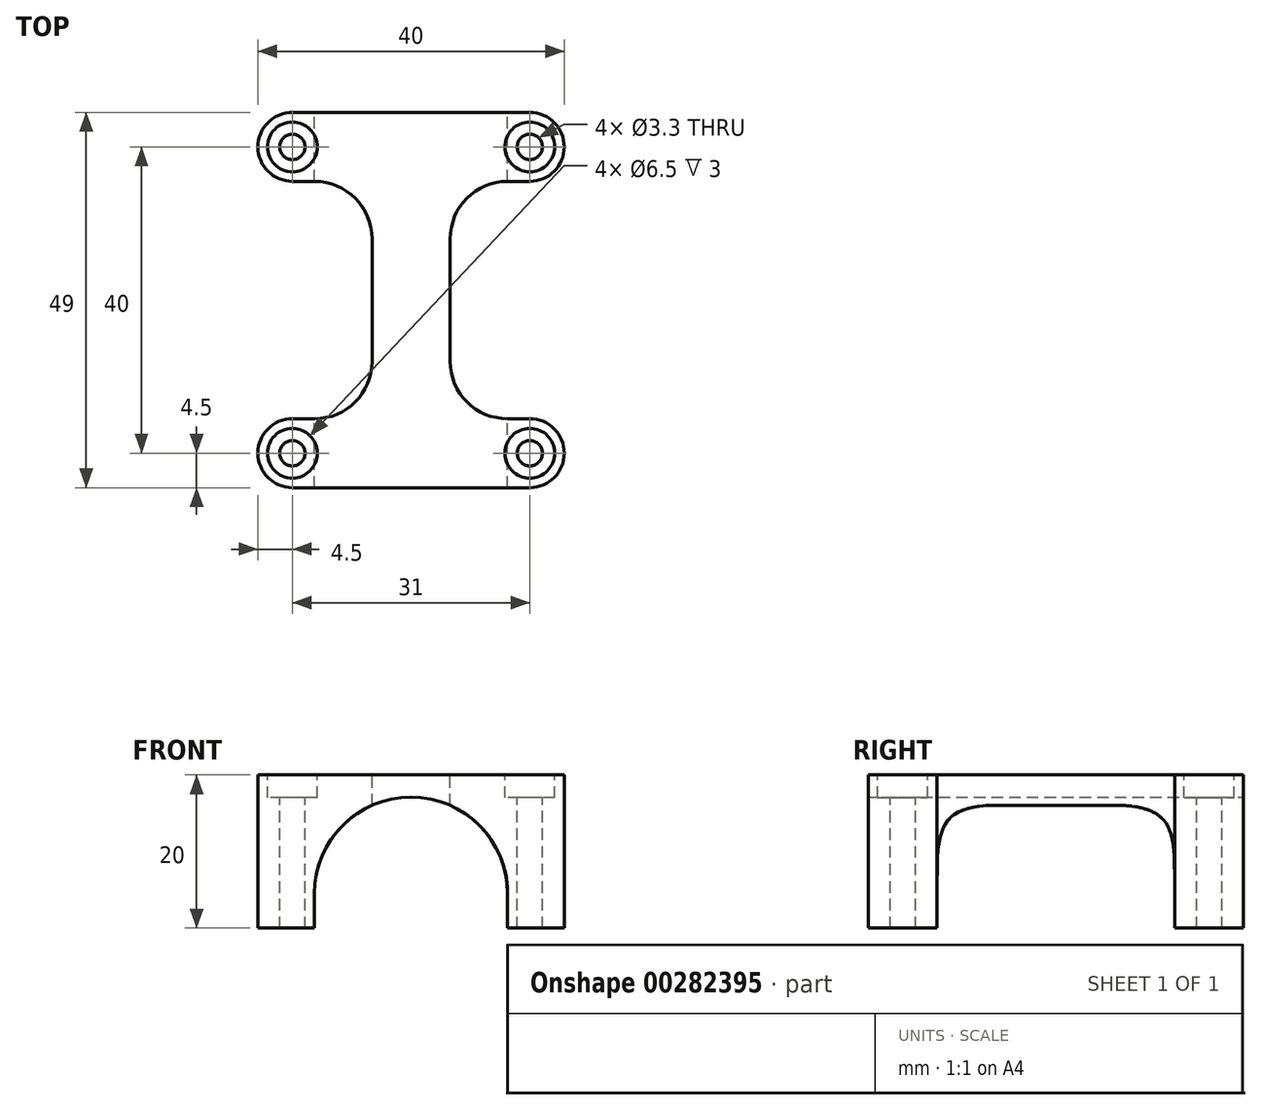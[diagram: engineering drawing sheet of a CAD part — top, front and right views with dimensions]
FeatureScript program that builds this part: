
annotation { "Feature Type Name" : "Feature", "Feature Type Description" : "" }
export const myFeature = defineFeature(function(context is Context, id is Id, definition is map)
    precondition{}
    {
        {
            var Q0;
            Q0=qCreatedBy(makeId("Front.planeOp"),FACE);
            var sketch = newSketch(context, id + "F0", { "sketchPlane" : qUnion([Q0])});
            skLineSegment(sketch, "E0.bottom", {"start": v(0, 0) * mm, "end": v(7.4, 0) * mm});
            skLineSegment(sketch, "E0.top", {"start": v(0, 20) * mm, "end": v(40, 20) * mm});
            skLineSegment(sketch, "E0.left", {"start": v(0, 0) * mm, "end": v(0, 20) * mm});
            skLineSegment(sketch, "E0.right", {"start": v(40, 0) * mm, "end": v(40, 20) * mm});
            skLineSegment(sketch, "E1", {"start": v(20, 20) * mm, "end": v(20, 4.5) * mm, "construction": true});
            skPoint(sketch, "E1.endSnap0", {"position": v(20, 0) * mm});
            skArc(sketch, "E2", {"start": v(32.6, 4.5) * mm, "mid": v(20, 17.1) * mm, "end": v(7.4, 4.5) * mm});
            skLineSegment(sketch, "E3.trimOffspring", {"start": v(32.6, 0) * mm, "end": v(40, 0) * mm});
            skLineSegment(sketch, "E4", {"start": v(7.4, 4.5) * mm, "end": v(7.4, 0) * mm});
            skLineSegment(sketch, "E5", {"start": v(32.6, 4.5) * mm, "end": v(32.6, 0) * mm});
            skSolve(sketch);
        }
        {
            var Q0;
            Q0=qSketchRegion(id+"F0",true);
            extrude(context, id + "F1", {"entities" : qUnion([Q0]), "depth" : 49 * mm});
        }
        {
            var Q0;
            Q0=makeQuery(id+"F1.opExtrude","SWEPT_FACE",FACE,{"disambiguationData":[OSD([sQuery(id+"F0.wireOp",EDGE,"E0.top")])]});
            var sketch = newSketch(context, id + "F2", { "sketchPlane" : qUnion([Q0])});
            skLineSegment(sketch, "E6", {"start": v(0, -24.5) * mm, "end": v(40, -24.5) * mm, "construction": true});
            skLineSegment(sketch, "E7", {"start": v(4.5, 0) * mm, "end": v(4.5, -49) * mm, "construction": true});
            skLineSegment(sketch, "E8", {"start": v(35.5, 0) * mm, "end": v(35.5, -49) * mm, "construction": true});
            skPoint(sketch, "E9", {"position": v(4.5, -4.5) * mm});
            skPoint(sketch, "E10", {"position": v(35.5, -4.5) * mm});
            skPoint(sketch, "E11", {"position": v(35.5, -44.5) * mm});
            skPoint(sketch, "E12", {"position": v(4.5, -44.5) * mm});
            skSolve(sketch);
        }
        {
            var Q0;
            Q0=sQuery(id+"F2.wireOp",VERTEX,"E9");
            var Q1;
            Q1=sQuery(id+"F2.wireOp",VERTEX,"E12");
            var Q2;
            Q2=sQuery(id+"F2.wireOp",VERTEX,"E11");
            var Q3;
            Q3=sQuery(id+"F2.wireOp",VERTEX,"E10");
            var Q4;
            Q4=makeQuery(id+"F1.opExtrude","SWEPT_BODY",BODY,{"disambiguationData":[OSD([sQuery(id+"F0.wireOp",EDGE,"E0.bottom"),sQuery(id+"F0.wireOp",EDGE,"E0.top"),sQuery(id+"F0.wireOp",EDGE,"E0.left"),sQuery(id+"F0.wireOp",EDGE,"E0.right"),sQuery(id+"F0.wireOp",EDGE,"E2"),sQuery(id+"F0.wireOp",EDGE,"E3.trimOffspring")])]});
            hole(context, id + "F3", {"style" : HoleStyle.C_BORE, "endStyle" : HoleEndStyle.BLIND, "standardTappedOrClearance" : lookupTablePath({ "standard" : "ISO", "fit" : "Normal", "size" : "M3", "type" : "Clearance" }), "standardBlindInLast" : lookupTablePath({ "fit" : "Standard", "standard" : "ISO", "size" : "M3", "type" : "Clearance" }), "holeDiameter" : 3.3 * mm, "cBoreDiameter" : 6.5 * mm, "cBoreDepth" : 3 * mm, "holeDepth" : 30 * mm, "tappedDepth" : 3 * mm, "tapClearance" : 3, "startFromSketch" : true, "locations" : qUnion([Q0, Q1, Q2, Q3]), "scope" : qUnion([Q4])});
        }
        {
            var Q0;
            Q0=makeQuery(id+"F1.opExtrude","SWEPT_FACE",FACE,{"disambiguationData":[OSD([sQuery(id+"F0.wireOp",EDGE,"E0.top")])]});
            var sketch = newSketch(context, id + "F4", { "sketchPlane" : qUnion([Q0])});
            skArc(sketch, "E13", {"start": v(14.9, -16.5) * mm, "mid": v(12.7, -11.2) * mm, "end": v(7.4, -9) * mm});
            skArc(sketch, "E14", {"start": v(7.4, -40) * mm, "mid": v(12.7, -37.8) * mm, "end": v(14.9, -32.5) * mm});
            skLineSegment(sketch, "E15", {"start": v(20, 0) * mm, "end": v(20, -49) * mm, "construction": true});
            skLineSegment(sketch, "E16", {"start": v(-0.1, -9) * mm, "end": v(-0.1, -40) * mm});
            skLineSegment(sketch, "E17", {"start": v(14.9, -16.5) * mm, "end": v(14.9, -32.5) * mm});
            skLineSegment(sketch, "E18", {"start": v(7.4, -16.5) * mm, "end": v(7.4, -32.5) * mm, "construction": true});
            skLineSegment(sketch, "E19", {"start": v(7.4, -9) * mm, "end": v(-0.1, -9) * mm});
            skLineSegment(sketch, "E20", {"start": v(7.4, -40) * mm, "end": v(-0.1, -40) * mm});
            skPoint(sketch, "E21.orphan", {"position": v(-0.1, -16.5) * mm});
            skPoint(sketch, "E22.orphan", {"position": v(-0.1, -32.5) * mm});
            skArc(sketch, "E23.MirrorCS", {"start": v(25.1, -16.5) * mm, "mid": v(27.3, -11.2) * mm, "end": v(32.6, -9) * mm});
            skLineSegment(sketch, "E24.MirrorCS", {"start": v(25.1, -16.5) * mm, "end": v(25.1, -32.5) * mm});
            skArc(sketch, "E25.MirrorCS", {"start": v(32.6, -40) * mm, "mid": v(27.3, -37.8) * mm, "end": v(25.1, -32.5) * mm});
            skLineSegment(sketch, "E26.MirrorCS", {"start": v(32.6, -40) * mm, "end": v(40.1, -40) * mm});
            skLineSegment(sketch, "E27.MirrorCS", {"start": v(40.1, -9) * mm, "end": v(40.1, -40) * mm});
            skLineSegment(sketch, "E28.MirrorCS", {"start": v(32.6, -9) * mm, "end": v(40.1, -9) * mm});
            skSolve(sketch);
        }
        {
            var Q0;
            Q0=qSketchRegion(id+"F4",true);
            extrude(context, id + "F5", {"entities" : qUnion([Q0]), "operationType" : NewBodyOperationType.REMOVE, "oppositeDirection" : true, "depth" : 25 * mm});
        }
        {
            var Q0;
            Q0=makeQuery(id+"F1.opExtrude","CAP_EDGE",EDGE,{"disambiguationData":[OSD([sQuery(id+"F0.wireOp",EDGE,"E0.right")])],"isStart":false});
            var Q1;
            Q1=makeQuery(id+"F1.opExtrude","CAP_EDGE",EDGE,{"disambiguationData":[OSD([sQuery(id+"F0.wireOp",EDGE,"E0.left")])],"isStart":false});
            var Q2;
            Q2=makeQuery(id+"F1.opExtrude","CAP_EDGE",EDGE,{"disambiguationData":[OSD([sQuery(id+"F0.wireOp",EDGE,"E0.right")])],"isStart":true});
            var Q3;
            Q3=makeQuery(id+"F1.opExtrude","CAP_EDGE",EDGE,{"disambiguationData":[OSD([sQuery(id+"F0.wireOp",EDGE,"E0.left")])],"isStart":true});
            var Q4;
            Q4=makeQuery(id+"F5.boolean.opBoolean","INTERSECT",EDGE,{"derivedFrom":[makeQuery(id+"F1.opExtrude","SWEPT_FACE",FACE,{"disambiguationData":[OSD([sQuery(id+"F0.wireOp",EDGE,"E0.right")])]}),makeQuery(id+"F5.opExtrude","SWEPT_FACE",FACE,{"disambiguationData":[OSD([sQuery(id+"F4.wireOp",EDGE,"E28.MirrorCS")])]})]});
            var Q5;
            Q5=makeQuery(id+"F5.boolean.opBoolean","INTERSECT",EDGE,{"derivedFrom":[makeQuery(id+"F1.opExtrude","SWEPT_FACE",FACE,{"disambiguationData":[OSD([sQuery(id+"F0.wireOp",EDGE,"E0.right")])]}),makeQuery(id+"F5.opExtrude","SWEPT_FACE",FACE,{"disambiguationData":[OSD([sQuery(id+"F4.wireOp",EDGE,"E26.MirrorCS")])]})]});
            var Q6;
            Q6=makeQuery(id+"F5.boolean.opBoolean","INTERSECT",EDGE,{"derivedFrom":[makeQuery(id+"F1.opExtrude","SWEPT_FACE",FACE,{"disambiguationData":[OSD([sQuery(id+"F0.wireOp",EDGE,"E0.left")])]}),makeQuery(id+"F5.opExtrude","SWEPT_FACE",FACE,{"disambiguationData":[OSD([sQuery(id+"F4.wireOp",EDGE,"E20")])]})]});
            var Q7;
            Q7=makeQuery(id+"F5.boolean.opBoolean","INTERSECT",EDGE,{"derivedFrom":[makeQuery(id+"F1.opExtrude","SWEPT_FACE",FACE,{"disambiguationData":[OSD([sQuery(id+"F0.wireOp",EDGE,"E0.left")])]}),makeQuery(id+"F5.opExtrude","SWEPT_FACE",FACE,{"disambiguationData":[OSD([sQuery(id+"F4.wireOp",EDGE,"E19")])]})]});
            fillet(context, id + "F6", {"entities" : qUnion([Q0, Q1, Q2, Q3, Q4, Q5, Q6, Q7]), "radius" : 4.5 * mm, "tangentPropagation" : true, "allowEdgeOverflow" : false});
        }
    });
